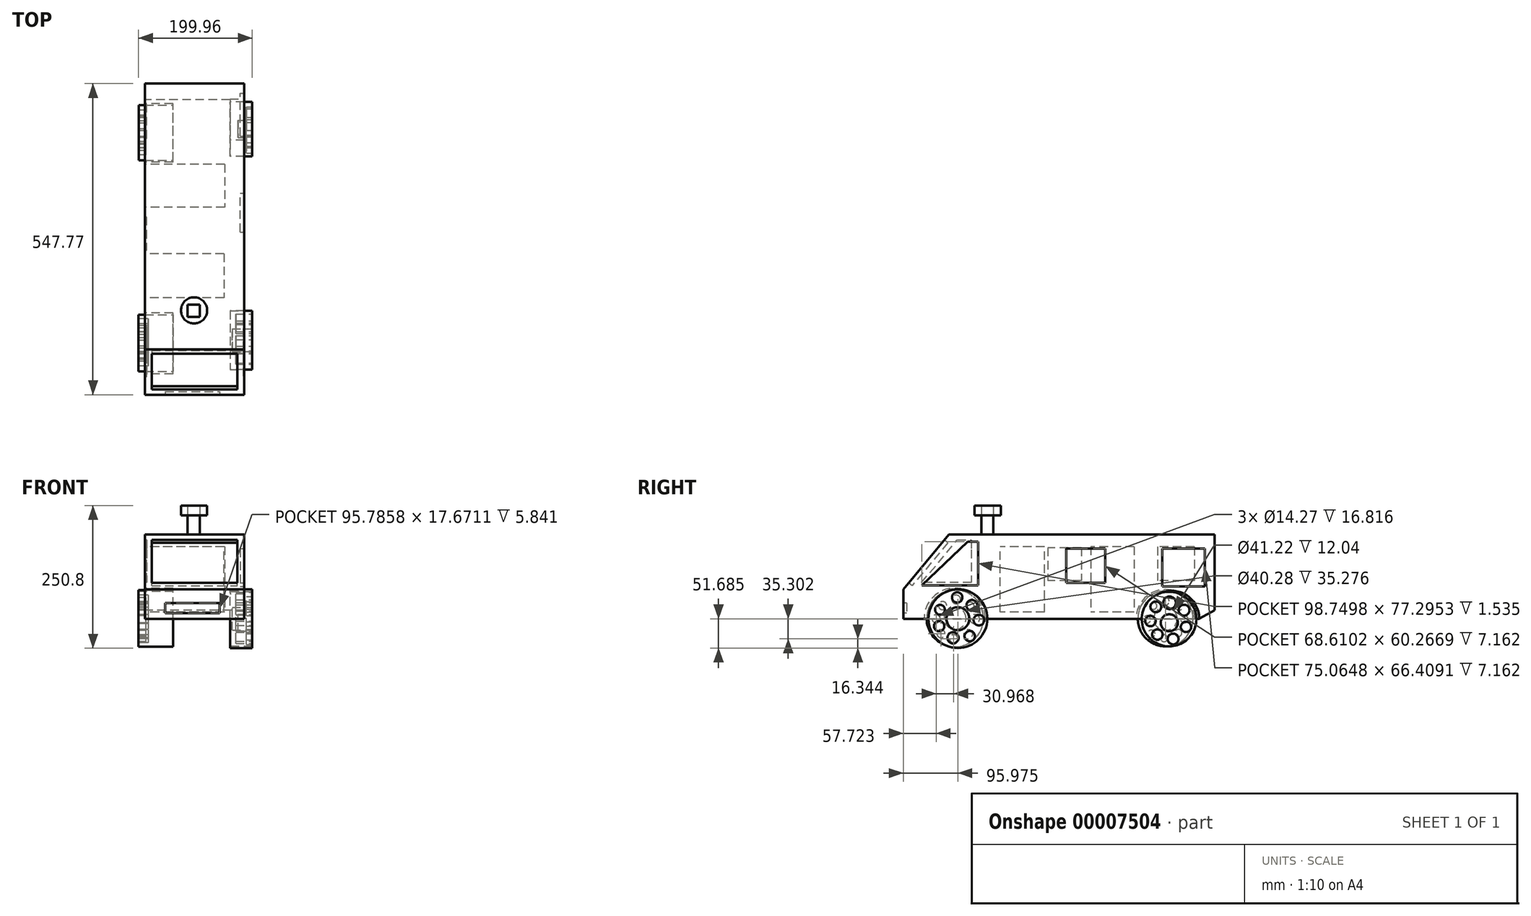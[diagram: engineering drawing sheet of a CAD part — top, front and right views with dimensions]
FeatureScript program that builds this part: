
annotation { "Feature Type Name" : "Feature", "Feature Type Description" : "" }
export const myFeature = defineFeature(function(context is Context, id is Id, definition is map)
    precondition{}
    {
        {
            var Q0;
            Q0=qCreatedBy(makeId("Front.planeOp"),FACE);
            var sketch = newSketch(context, id + "F0", { "sketchPlane" : qUnion([Q0])});
            skLineSegment(sketch, "E0.bottom", {"start": v(74.37, 73.44) * mm, "end": v(-75.3, 73.44) * mm});
            skLineSegment(sketch, "E0.top", {"start": v(74.37, -74.82) * mm, "end": v(-75.3, -74.82) * mm});
            skLineSegment(sketch, "E0.left", {"start": v(74.37, 73.44) * mm, "end": v(74.37, -74.82) * mm});
            skLineSegment(sketch, "E0.right", {"start": v(-75.3, 73.44) * mm, "end": v(-75.3, -74.82) * mm});
            skSolve(sketch);
        }
        {
            var Q0;
            Q0=makeQuery(id+"F0.imprint","IMPRINT",FACE,{"disambiguationData":[TD([[makeQuery(id+"F0.imprint","IMPRINT",EDGE,{"derivedFrom":sQuery(id+"F0.wireOp",EDGE,"E0.bottom")}),1.0]])]});
            extrude(context, id + "F1", {"entities" : qUnion([Q0]), "depth" : 547.77 * mm});
        }
        {
            var Q0;
            Q0=makeQuery(id+"F1.opExtrude","SWEPT_FACE",FACE,{"disambiguationData":[OSD([sQuery(id+"F0.wireOp",EDGE,"E0.right")])]});
            var sketch = newSketch(context, id + "F2", { "sketchPlane" : qUnion([Q0])});
            skCircle(sketch, "E1", {"center": v(86.72, -74.82) * mm, "radius": 51.51 * mm});
            skCircle(sketch, "E2", {"center": v(457.4, -74.82) * mm, "radius": 53.88 * mm});
            skSolve(sketch);
        }
        {
            var Q0;
            {var subQ0=makeQuery(id+"F1.opExtrude","SWEPT_EDGE",EDGE,{"disambiguationData":[OSD([sQuery(id+"F0.wireOp",EDGE,"E0.top"),sQuery(id+"F0.wireOp",EDGE,"E0.right")])]});var subQ1=sQuery(id+"F2.wireOp",EDGE,"E1");var subQ3=makeQuery(id+"F2.imprint","INTERSECT",VERTEX,{"disambiguationData":[OD(0.0)],"derivedFrom":[subQ0,subQ1]});Q0=makeQuery(id+"F2.imprint","IMPRINT",FACE,{"disambiguationData":[TD([[makeQuery(id+"F2.imprint","IMPRINT",EDGE,{"disambiguationData":[TD([[subQ3,-1.0]])],"derivedFrom":subQ1}),1.0]])]});}
            var Q1;
            {var subQ0=makeQuery(id+"F1.opExtrude","SWEPT_EDGE",EDGE,{"disambiguationData":[OSD([sQuery(id+"F0.wireOp",EDGE,"E0.top"),sQuery(id+"F0.wireOp",EDGE,"E0.right")])]});var subQ1=sQuery(id+"F2.wireOp",EDGE,"E1");var subQ3=makeQuery(id+"F2.imprint","INTERSECT",VERTEX,{"disambiguationData":[OD(0.0)],"derivedFrom":[subQ0,subQ1]});Q1=makeQuery(id+"F2.imprint","IMPRINT",FACE,{"disambiguationData":[TD([[makeQuery(id+"F2.imprint","IMPRINT",EDGE,{"disambiguationData":[TD([[subQ3,1.0]])],"derivedFrom":subQ1}),1.0]])]});}
            var Q2;
            {var subQ0=makeQuery(id+"F1.opExtrude","SWEPT_EDGE",EDGE,{"disambiguationData":[OSD([sQuery(id+"F0.wireOp",EDGE,"E0.top"),sQuery(id+"F0.wireOp",EDGE,"E0.right")])]});var subQ1=sQuery(id+"F2.wireOp",EDGE,"E2");var subQ3=makeQuery(id+"F2.imprint","INTERSECT",VERTEX,{"disambiguationData":[OD(0.0)],"derivedFrom":[subQ0,subQ1]});Q2=makeQuery(id+"F2.imprint","IMPRINT",FACE,{"disambiguationData":[TD([[makeQuery(id+"F2.imprint","IMPRINT",EDGE,{"disambiguationData":[TD([[subQ3,1.0]])],"derivedFrom":subQ1}),1.0]])]});}
            var Q3;
            {var subQ0=makeQuery(id+"F1.opExtrude","SWEPT_EDGE",EDGE,{"disambiguationData":[OSD([sQuery(id+"F0.wireOp",EDGE,"E0.top"),sQuery(id+"F0.wireOp",EDGE,"E0.right")])]});var subQ1=sQuery(id+"F2.wireOp",EDGE,"E2");var subQ3=makeQuery(id+"F2.imprint","INTERSECT",VERTEX,{"disambiguationData":[OD(0.0)],"derivedFrom":[subQ0,subQ1]});Q3=makeQuery(id+"F2.imprint","IMPRINT",FACE,{"disambiguationData":[TD([[makeQuery(id+"F2.imprint","IMPRINT",EDGE,{"disambiguationData":[TD([[subQ3,-1.0]])],"derivedFrom":subQ1}),1.0]])]});}
            extrude(context, id + "F3", {"entities" : qUnion([Q0, Q1, Q2, Q3]), "operationType" : NewBodyOperationType.REMOVE, "oppositeDirection" : true, "depth" : 24.2 * mm});
        }
        {
            var Q0;
            Q0=makeQuery(id+"F3.boolean.opBoolean","COPY",FACE,{"derivedFrom":makeQuery(id+"F3.opExtrude","CAP_FACE",FACE,{"disambiguationData":[OSD([sQuery(id+"F2.wireOp",EDGE,"E1")])],"isStart":false})});
            var sketch = newSketch(context, id + "F4", { "sketchPlane" : qUnion([Q0])});
            skCircle(sketch, "E3", {"center": v(86.72, -74.82) * mm, "radius": 48.61 * mm});
            skCircle(sketch, "E4", {"center": v(456.68, -74.24) * mm, "radius": 49.9 * mm});
            skSolve(sketch);
        }
        {
            var Q0;
            {var subQ0=makeQuery(id+"F3.boolean.opBoolean","INTERSECT",EDGE,{"derivedFrom":[makeQuery(id+"F1.opExtrude","SWEPT_FACE",FACE,{"disambiguationData":[OSD([sQuery(id+"F0.wireOp",EDGE,"E0.top")])]}),makeQuery(id+"F3.opExtrude","CAP_FACE",FACE,{"disambiguationData":[OSD([sQuery(id+"F2.wireOp",EDGE,"E1")])],"isStart":false})]});var subQ1=sQuery(id+"F4.wireOp",EDGE,"E3");var subQ3=makeQuery(id+"F4.imprint","INTERSECT",VERTEX,{"disambiguationData":[OD(0.0)],"derivedFrom":[subQ0,subQ1]});Q0=makeQuery(id+"F4.imprint","IMPRINT",FACE,{"disambiguationData":[TD([[makeQuery(id+"F4.imprint","IMPRINT",EDGE,{"disambiguationData":[TD([[subQ3,1.0]])],"derivedFrom":subQ1}),1.0]])]});}
            var Q1;
            {var subQ0=makeQuery(id+"F3.boolean.opBoolean","INTERSECT",EDGE,{"derivedFrom":[makeQuery(id+"F1.opExtrude","SWEPT_FACE",FACE,{"disambiguationData":[OSD([sQuery(id+"F0.wireOp",EDGE,"E0.top")])]}),makeQuery(id+"F3.opExtrude","CAP_FACE",FACE,{"disambiguationData":[OSD([sQuery(id+"F2.wireOp",EDGE,"E1")])],"isStart":false})]});var subQ1=sQuery(id+"F4.wireOp",EDGE,"E3");var subQ3=makeQuery(id+"F4.imprint","INTERSECT",VERTEX,{"disambiguationData":[OD(0.0)],"derivedFrom":[subQ0,subQ1]});Q1=makeQuery(id+"F4.imprint","IMPRINT",FACE,{"disambiguationData":[TD([[makeQuery(id+"F4.imprint","IMPRINT",EDGE,{"disambiguationData":[TD([[subQ3,-1.0]])],"derivedFrom":subQ1}),1.0]])]});}
            var Q2;
            Q2=makeQuery(id+"F4.imprint","IMPRINT",FACE,{"disambiguationData":[TD([[makeQuery(id+"F4.imprint","IMPRINT",EDGE,{"derivedFrom":sQuery(id+"F4.wireOp",EDGE,"E4")}),1.0]])]});
            extrude(context, id + "F5", {"entities" : qUnion([Q0, Q1, Q2]), "operationType" : NewBodyOperationType.ADD, "depth" : 40.9 * mm});
        }
        {
            var Q0;
            Q0=makeQuery(id+"F1.opExtrude","SWEPT_FACE",FACE,{"disambiguationData":[OSD([sQuery(id+"F0.wireOp",EDGE,"E0.left")])]});
            var sketch = newSketch(context, id + "F6", { "sketchPlane" : qUnion([Q0])});
            skCircle(sketch, "E5", {"center": v(-451.8, -74.82) * mm, "radius": 51.88 * mm});
            skCircle(sketch, "E6", {"center": v(-76.52, -74.82) * mm, "radius": 49.33 * mm});
            skSolve(sketch);
        }
        {
            var Q0;
            {var subQ0=makeQuery(id+"F1.opExtrude","SWEPT_EDGE",EDGE,{"disambiguationData":[OSD([sQuery(id+"F0.wireOp",EDGE,"E0.top"),sQuery(id+"F0.wireOp",EDGE,"E0.left")])]});var subQ1=sQuery(id+"F6.wireOp",EDGE,"E5");var subQ3=makeQuery(id+"F6.imprint","INTERSECT",VERTEX,{"disambiguationData":[OD(0.0)],"derivedFrom":[subQ0,subQ1]});Q0=makeQuery(id+"F6.imprint","IMPRINT",FACE,{"disambiguationData":[TD([[makeQuery(id+"F6.imprint","IMPRINT",EDGE,{"disambiguationData":[TD([[subQ3,1.0]])],"derivedFrom":subQ1}),1.0]])]});}
            var Q1;
            {var subQ0=makeQuery(id+"F1.opExtrude","SWEPT_EDGE",EDGE,{"disambiguationData":[OSD([sQuery(id+"F0.wireOp",EDGE,"E0.top"),sQuery(id+"F0.wireOp",EDGE,"E0.left")])]});var subQ1=sQuery(id+"F6.wireOp",EDGE,"E6");var subQ3=makeQuery(id+"F6.imprint","INTERSECT",VERTEX,{"disambiguationData":[OD(0.0)],"derivedFrom":[subQ0,subQ1]});Q1=makeQuery(id+"F6.imprint","IMPRINT",FACE,{"disambiguationData":[TD([[makeQuery(id+"F6.imprint","IMPRINT",EDGE,{"disambiguationData":[TD([[subQ3,-1.0]])],"derivedFrom":subQ1}),1.0]])]});}
            var Q2;
            {var subQ0=makeQuery(id+"F1.opExtrude","SWEPT_EDGE",EDGE,{"disambiguationData":[OSD([sQuery(id+"F0.wireOp",EDGE,"E0.top"),sQuery(id+"F0.wireOp",EDGE,"E0.left")])]});var subQ1=sQuery(id+"F6.wireOp",EDGE,"E6");var subQ3=makeQuery(id+"F6.imprint","INTERSECT",VERTEX,{"disambiguationData":[OD(0.0)],"derivedFrom":[subQ0,subQ1]});Q2=makeQuery(id+"F6.imprint","IMPRINT",FACE,{"disambiguationData":[TD([[makeQuery(id+"F6.imprint","IMPRINT",EDGE,{"disambiguationData":[TD([[subQ3,1.0]])],"derivedFrom":subQ1}),1.0]])]});}
            var Q3;
            {var subQ0=makeQuery(id+"F1.opExtrude","SWEPT_EDGE",EDGE,{"disambiguationData":[OSD([sQuery(id+"F0.wireOp",EDGE,"E0.top"),sQuery(id+"F0.wireOp",EDGE,"E0.left")])]});var subQ1=sQuery(id+"F6.wireOp",EDGE,"E5");var subQ3=makeQuery(id+"F6.imprint","INTERSECT",VERTEX,{"disambiguationData":[OD(0.0)],"derivedFrom":[subQ0,subQ1]});Q3=makeQuery(id+"F6.imprint","IMPRINT",FACE,{"disambiguationData":[TD([[makeQuery(id+"F6.imprint","IMPRINT",EDGE,{"disambiguationData":[TD([[subQ3,-1.0]])],"derivedFrom":subQ1}),1.0]])]});}
            extrude(context, id + "F7", {"entities" : qUnion([Q0, Q1, Q2, Q3]), "operationType" : NewBodyOperationType.REMOVE, "oppositeDirection" : true, "depth" : 25 * mm});
        }
        {
            var Q0;
            Q0=makeQuery(id+"F7.boolean.opBoolean","COPY",FACE,{"derivedFrom":makeQuery(id+"F7.opExtrude","CAP_FACE",FACE,{"disambiguationData":[OSD([sQuery(id+"F6.wireOp",EDGE,"E5")])],"isStart":false})});
            var sketch = newSketch(context, id + "F8", { "sketchPlane" : qUnion([Q0])});
            skCircle(sketch, "E7", {"center": v(-451.8, -74.82) * mm, "radius": 51.69 * mm});
            skCircle(sketch, "E8", {"center": v(-80.35, -75.29) * mm, "radius": 48.09 * mm});
            skSolve(sketch);
        }
        {
            var Q0;
            {var subQ0=makeQuery(id+"F7.boolean.opBoolean","INTERSECT",EDGE,{"derivedFrom":[makeQuery(id+"F1.opExtrude","SWEPT_FACE",FACE,{"disambiguationData":[OSD([sQuery(id+"F0.wireOp",EDGE,"E0.top")])]}),makeQuery(id+"F7.opExtrude","CAP_FACE",FACE,{"disambiguationData":[OSD([sQuery(id+"F6.wireOp",EDGE,"E5")])],"isStart":false})]});var subQ1=sQuery(id+"F8.wireOp",EDGE,"E7");var subQ3=makeQuery(id+"F8.imprint","INTERSECT",VERTEX,{"disambiguationData":[OD(0.0)],"derivedFrom":[subQ0,subQ1]});Q0=makeQuery(id+"F8.imprint","IMPRINT",FACE,{"disambiguationData":[TD([[makeQuery(id+"F8.imprint","IMPRINT",EDGE,{"disambiguationData":[TD([[subQ3,-1.0]])],"derivedFrom":subQ1}),1.0]])]});}
            var Q1;
            {var subQ0=makeQuery(id+"F7.boolean.opBoolean","INTERSECT",EDGE,{"derivedFrom":[makeQuery(id+"F1.opExtrude","SWEPT_FACE",FACE,{"disambiguationData":[OSD([sQuery(id+"F0.wireOp",EDGE,"E0.top")])]}),makeQuery(id+"F7.opExtrude","CAP_FACE",FACE,{"disambiguationData":[OSD([sQuery(id+"F6.wireOp",EDGE,"E5")])],"isStart":false})]});var subQ1=sQuery(id+"F8.wireOp",EDGE,"E7");var subQ3=makeQuery(id+"F8.imprint","INTERSECT",VERTEX,{"disambiguationData":[OD(0.0)],"derivedFrom":[subQ0,subQ1]});Q1=makeQuery(id+"F8.imprint","IMPRINT",FACE,{"disambiguationData":[TD([[makeQuery(id+"F8.imprint","IMPRINT",EDGE,{"disambiguationData":[TD([[subQ3,1.0]])],"derivedFrom":subQ1}),1.0]])]});}
            var Q2;
            Q2=makeQuery(id+"F8.imprint","IMPRINT",FACE,{"disambiguationData":[TD([[makeQuery(id+"F8.imprint","IMPRINT",EDGE,{"derivedFrom":sQuery(id+"F8.wireOp",EDGE,"E8")}),1.0]])]});
            extrude(context, id + "F9", {"entities" : qUnion([Q0, Q1, Q2]), "operationType" : NewBodyOperationType.ADD, "depth" : 39 * mm});
        }
        {
            var Q0;
            Q0=makeQuery(id+"F1.opExtrude","SWEPT_FACE",FACE,{"disambiguationData":[OSD([sQuery(id+"F0.wireOp",EDGE,"E0.right")])]});
            var sketch = newSketch(context, id + "F10", { "sketchPlane" : qUnion([Q0])});
            skLineSegment(sketch, "E9", {"start": v(467.77, 73.44) * mm, "end": v(547.77, -22.84) * mm});
            skLineSegment(sketch, "E10", {"start": v(547.77, -22.84) * mm, "end": v(547.77, 73.44) * mm});
            skLineSegment(sketch, "E11", {"start": v(547.77, 73.44) * mm, "end": v(467.77, 73.44) * mm});
            skSolve(sketch);
        }
        {
            var Q0;
            Q0=makeQuery(id+"F10.imprint","IMPRINT",FACE,{"disambiguationData":[TD([[makeQuery(id+"F10.imprint","IMPRINT",EDGE,{"derivedFrom":sQuery(id+"F10.wireOp",EDGE,"E9")}),1.0]])]});
            extrude(context, id + "F11", {"entities" : qUnion([Q0]), "operationType" : NewBodyOperationType.REMOVE, "oppositeDirection" : true, "depth" : 194.14 * mm});
        }
        {
            var Q0;
            Q0=makeQuery(id+"F1.opExtrude","SWEPT_FACE",FACE,{"disambiguationData":[OSD([sQuery(id+"F0.wireOp",EDGE,"E0.right")])]});
            var sketch = newSketch(context, id + "F12", { "sketchPlane" : qUnion([Q0])});
            skSolve(sketch);
        }
        {
            var Q0;
            {var subQ0=sQuery(id+"F0.wireOp",EDGE,"E0.right");Q0=makeQuery(id+"F12.imprint","IMPRINT",FACE,{"disambiguationData":[TD([[makeQuery(id+"F12.imprint","IMPRINT",EDGE,{"derivedFrom":makeQuery(id+"F1.opExtrude","CAP_EDGE",EDGE,{"disambiguationData":[OSD([subQ0])],"isStart":true})}),1.0]])]});}
            var sketch = newSketch(context, id + "F13", { "sketchPlane" : qUnion([Q0])});
            skLineSegment(sketch, "E12.bottom", {"start": v(299.28, -63.26) * mm, "end": v(377.16, -63.26) * mm});
            skLineSegment(sketch, "E12.top", {"start": v(299.28, 51.97) * mm, "end": v(377.16, 51.97) * mm});
            skLineSegment(sketch, "E12.left", {"start": v(299.28, -63.26) * mm, "end": v(299.28, 51.97) * mm});
            skLineSegment(sketch, "E12.right", {"start": v(377.16, -63.26) * mm, "end": v(377.16, 51.97) * mm});
            skSolve(sketch);
        }
        {
            var Q0;
            Q0=makeQuery(id+"F13.imprint","IMPRINT",FACE,{"disambiguationData":[TD([[makeQuery(id+"F13.imprint","IMPRINT",EDGE,{"derivedFrom":sQuery(id+"F13.wireOp",EDGE,"E12.bottom")}),1.0]])]});
            extrude(context, id + "F14", {"entities" : qUnion([Q0]), "operationType" : NewBodyOperationType.REMOVE, "oppositeDirection" : true, "depth" : 147.5 * mm});
        }
        {
            var Q0;
            Q0=makeQuery(id+"F1.opExtrude","SWEPT_FACE",FACE,{"disambiguationData":[OSD([sQuery(id+"F0.wireOp",EDGE,"E0.right")])]});
            extrude(context, id + "F15", {"entities" : qUnion([Q0]), "operationType" : NewBodyOperationType.ADD, "depth" : 25 * mm});
        }
        {
            var Q0;
            Q0=makeQuery(id+"F15.opExtrude","CAP_FACE",FACE,{"disambiguationData":[OSD([sQuery(id+"F0.wireOp",EDGE,"E0.right")])],"isStart":false});
            var sketch = newSketch(context, id + "F16", { "sketchPlane" : qUnion([Q0])});
            skLineSegment(sketch, "E13.bottom", {"start": v(141.83, 51.97) * mm, "end": v(217.84, 51.97) * mm});
            skLineSegment(sketch, "E13.top", {"start": v(141.83, -63.26) * mm, "end": v(217.84, -63.26) * mm});
            skLineSegment(sketch, "E13.left", {"start": v(141.83, 51.97) * mm, "end": v(141.83, -63.26) * mm});
            skLineSegment(sketch, "E13.right", {"start": v(217.84, 51.97) * mm, "end": v(217.84, -63.26) * mm});
            skSolve(sketch);
        }
        {
            var Q0;
            Q0=makeQuery(id+"F16.imprint","IMPRINT",FACE,{"disambiguationData":[TD([[makeQuery(id+"F16.imprint","IMPRINT",EDGE,{"derivedFrom":sQuery(id+"F16.wireOp",EDGE,"E13.bottom")}),-1.0]])]});
            extrude(context, id + "F17", {"entities" : qUnion([Q0]), "operationType" : NewBodyOperationType.REMOVE, "oppositeDirection" : true, "depth" : 173.86 * mm});
        }
        {
            var Q0;
            Q0=makeQuery(id+"F5.opExtrude","CAP_FACE",FACE,{"disambiguationData":[OSD([sQuery(id+"F4.wireOp",EDGE,"E3")])],"isStart":false});
            extrude(context, id + "F18", {"entities" : qUnion([Q0]), "operationType" : NewBodyOperationType.ADD, "depth" : 19.4 * mm});
        }
        {
            var Q0;
            Q0=makeQuery(id+"F5.opExtrude","CAP_FACE",FACE,{"disambiguationData":[OSD([sQuery(id+"F4.wireOp",EDGE,"E4")])],"isStart":false});
            extrude(context, id + "F19", {"entities" : qUnion([Q0]), "operationType" : NewBodyOperationType.ADD, "depth" : 19.6 * mm});
        }
        {
            var Q0;
            {var subQ0=sQuery(id+"F10.wireOp",EDGE,"E9");Q0=makeQuery(id+"F15.boolean.opBoolean","MERGE",FACE,{"derivedFrom":[makeQuery(id+"F11.boolean.opBoolean","COPY",FACE,{"derivedFrom":makeQuery(id+"F11.opExtrude","SWEPT_FACE",FACE,{"disambiguationData":[OSD([subQ0])]})}),makeQuery(id+"F15.opExtrude","SWEPT_FACE",FACE,{"disambiguationData":[OSD([subQ0])]})]});}
            var sketch = newSketch(context, id + "F20", { "sketchPlane" : qUnion([Q0])});
            skLineSegment(sketch, "E14.bottom", {"start": v(-88.12, -254.66) * mm, "end": v(62.1, -254.66) * mm});
            skLineSegment(sketch, "E14.top", {"start": v(-88.12, -353.33) * mm, "end": v(62.1, -353.33) * mm});
            skLineSegment(sketch, "E14.left", {"start": v(-88.12, -254.66) * mm, "end": v(-88.12, -353.33) * mm});
            skLineSegment(sketch, "E14.right", {"start": v(62.1, -254.66) * mm, "end": v(62.1, -353.33) * mm});
            skSolve(sketch);
        }
        {
            var Q0;
            Q0=makeQuery(id+"F20.imprint","IMPRINT",FACE,{"disambiguationData":[TD([[makeQuery(id+"F20.imprint","IMPRINT",EDGE,{"derivedFrom":sQuery(id+"F20.wireOp",EDGE,"E14.bottom")}),-1.0]])]});
            extrude(context, id + "F21", {"entities" : qUnion([Q0]), "operationType" : NewBodyOperationType.REMOVE, "oppositeDirection" : true, "depth" : 7.95 * mm});
        }
        {
            var Q0;
            Q0=makeQuery(id+"F17.boolean.opBoolean","COPY",FACE,{"derivedFrom":makeQuery(id+"F17.opExtrude","CAP_FACE",FACE,{"disambiguationData":[OSD([sQuery(id+"F16.wireOp",EDGE,"E13.bottom"),sQuery(id+"F16.wireOp",EDGE,"E13.top"),sQuery(id+"F16.wireOp",EDGE,"E13.left"),sQuery(id+"F16.wireOp",EDGE,"E13.right")])],"isStart":false})});
            var sketch = newSketch(context, id + "F22", { "sketchPlane" : qUnion([Q0])});
            skLineSegment(sketch, "E15.bottom", {"start": v(217.84, 51.97) * mm, "end": v(141.83, 51.97) * mm});
            skLineSegment(sketch, "E15.top", {"start": v(217.84, -63.26) * mm, "end": v(141.83, -63.26) * mm});
            skLineSegment(sketch, "E15.left", {"start": v(217.84, 51.97) * mm, "end": v(217.84, -63.26) * mm});
            skLineSegment(sketch, "E15.right", {"start": v(141.83, 51.97) * mm, "end": v(141.83, -63.26) * mm});
            skSolve(sketch);
        }
        {
            var Q0;
            Q0=makeQuery(id+"F14.boolean.opBoolean","COPY",FACE,{"derivedFrom":makeQuery(id+"F14.opExtrude","CAP_FACE",FACE,{"disambiguationData":[OSD([sQuery(id+"F13.wireOp",EDGE,"E12.bottom"),sQuery(id+"F13.wireOp",EDGE,"E12.top"),sQuery(id+"F13.wireOp",EDGE,"E12.left"),sQuery(id+"F13.wireOp",EDGE,"E12.right")])],"isStart":false})});
            var sketch = newSketch(context, id + "F23", { "sketchPlane" : qUnion([Q0])});
            skLineSegment(sketch, "E16.bottom", {"start": v(377.16, 51.97) * mm, "end": v(299.28, 51.97) * mm});
            skLineSegment(sketch, "E16.top", {"start": v(377.16, -63.26) * mm, "end": v(299.28, -63.26) * mm});
            skLineSegment(sketch, "E16.left", {"start": v(377.16, 51.97) * mm, "end": v(377.16, -63.26) * mm});
            skLineSegment(sketch, "E16.right", {"start": v(299.28, 51.97) * mm, "end": v(299.28, -63.26) * mm});
            skSolve(sketch);
        }
        {
            var Q0;
            Q0=makeQuery(id+"F23.imprint","IMPRINT",FACE,{"disambiguationData":[TD([[makeQuery(id+"F23.imprint","IMPRINT",EDGE,{"derivedFrom":sQuery(id+"F23.wireOp",EDGE,"E16.bottom")}),-1.0]])]});
            var Q1;
            Q1=makeQuery(id+"F22.imprint","IMPRINT",FACE,{"disambiguationData":[TD([[makeQuery(id+"F22.imprint","IMPRINT",EDGE,{"derivedFrom":sQuery(id+"F22.wireOp",EDGE,"E15.bottom")}),-1.0]])]});
            extrude(context, id + "F24", {"entities" : qUnion([Q0, Q1]), "operationType" : NewBodyOperationType.ADD, "depth" : 33.55 * mm});
        }
        {
            var Q0;
            {var subQ0=sQuery(id+"F0.wireOp",EDGE,"E0.bottom");Q0=makeQuery(id+"F15.boolean.opBoolean","MERGE",FACE,{"derivedFrom":[makeQuery(id+"F1.opExtrude","SWEPT_FACE",FACE,{"disambiguationData":[OSD([subQ0])]}),makeQuery(id+"F15.opExtrude","SWEPT_FACE",FACE,{"disambiguationData":[OSD([subQ0,sQuery(id+"F0.wireOp",EDGE,"E0.right")])]})]});}
            var sketch = newSketch(context, id + "F25", { "sketchPlane" : qUnion([Q0])});
            skLineSegment(sketch, "E17.bottom", {"start": v(-4.06, -389.3) * mm, "end": v(-25.31, -389.3) * mm});
            skLineSegment(sketch, "E17.top", {"start": v(-4.06, -410.41) * mm, "end": v(-25.31, -410.41) * mm});
            skLineSegment(sketch, "E17.left", {"start": v(-4.06, -389.3) * mm, "end": v(-4.06, -410.41) * mm});
            skLineSegment(sketch, "E17.right", {"start": v(-25.31, -389.3) * mm, "end": v(-25.31, -410.41) * mm});
            skSolve(sketch);
        }
        {
            var Q0;
            Q0=makeQuery(id+"F25.imprint","IMPRINT",FACE,{"disambiguationData":[TD([[makeQuery(id+"F25.imprint","IMPRINT",EDGE,{"derivedFrom":sQuery(id+"F25.wireOp",EDGE,"E17.bottom")}),1.0]])]});
            extrude(context, id + "F26", {"entities" : qUnion([Q0]), "operationType" : NewBodyOperationType.ADD, "depth" : 33.85 * mm});
        }
        {
            var Q0;
            Q0=makeQuery(id+"F26.opExtrude","CAP_FACE",FACE,{"disambiguationData":[OSD([sQuery(id+"F25.wireOp",EDGE,"E17.bottom"),sQuery(id+"F25.wireOp",EDGE,"E17.top"),sQuery(id+"F25.wireOp",EDGE,"E17.left"),sQuery(id+"F25.wireOp",EDGE,"E17.right")])],"isStart":false});
            var sketch = newSketch(context, id + "F27", { "sketchPlane" : qUnion([Q0])});
            skCircle(sketch, "E18", {"center": v(-13.96, -399.18) * mm, "radius": 23.07 * mm});
            skSolve(sketch);
        }
        {
            var Q0;
            Q0=makeQuery(id+"F27.imprint","IMPRINT",FACE,{"disambiguationData":[TD([[makeQuery(id+"F27.imprint","IMPRINT",EDGE,{"derivedFrom":sQuery(id+"F27.wireOp",EDGE,"E18")}),1.0]])]});
            extrude(context, id + "F28", {"entities" : qUnion([Q0]), "depth" : 17 * mm});
        }
        {
            var Q0;
            {var subQ0=sQuery(id+"F0.wireOp",EDGE,"E0.right");Q0=makeQuery(id+"F15.boolean.opBoolean","MERGE",FACE,{"derivedFrom":[makeQuery(id+"F1.opExtrude","CAP_FACE",FACE,{"disambiguationData":[OSD([sQuery(id+"F0.wireOp",EDGE,"E0.bottom"),sQuery(id+"F0.wireOp",EDGE,"E0.top"),sQuery(id+"F0.wireOp",EDGE,"E0.left"),subQ0])],"isStart":false}),makeQuery(id+"F15.opExtrude","SWEPT_FACE",FACE,{"disambiguationData":[OSD([subQ0]),TDD([makeQuery(id+"F1.opExtrude","CAP_EDGE",EDGE,{"disambiguationData":[OSD([subQ0])],"isStart":false})])]})]});}
            var sketch = newSketch(context, id + "F29", { "sketchPlane" : qUnion([Q0])});
            skLineSegment(sketch, "E19.bottom", {"start": v(-64.55, -47) * mm, "end": v(31.24, -47) * mm});
            skLineSegment(sketch, "E19.top", {"start": v(-64.55, -64.68) * mm, "end": v(31.24, -64.68) * mm});
            skLineSegment(sketch, "E19.left", {"start": v(-64.55, -47) * mm, "end": v(-64.55, -64.68) * mm});
            skLineSegment(sketch, "E19.right", {"start": v(31.24, -47) * mm, "end": v(31.24, -64.68) * mm});
            skSolve(sketch);
        }
        {
            var Q0;
            Q0=makeQuery(id+"F29.imprint","IMPRINT",FACE,{"disambiguationData":[TD([[makeQuery(id+"F29.imprint","IMPRINT",EDGE,{"derivedFrom":sQuery(id+"F29.wireOp",EDGE,"E19.bottom")}),-1.0]])]});
            extrude(context, id + "F30", {"entities" : qUnion([Q0]), "operationType" : NewBodyOperationType.REMOVE, "oppositeDirection" : true, "depth" : 5.84 * mm});
        }
        {
            var Q0;
            Q0=makeQuery(id+"F26.opExtrude","CAP_FACE",FACE,{"disambiguationData":[OSD([sQuery(id+"F25.wireOp",EDGE,"E17.bottom"),sQuery(id+"F25.wireOp",EDGE,"E17.top"),sQuery(id+"F25.wireOp",EDGE,"E17.left"),sQuery(id+"F25.wireOp",EDGE,"E17.right")])],"isStart":false});
            var sketch = newSketch(context, id + "F31", { "sketchPlane" : qUnion([Q0])});
            skLineSegment(sketch, "E20.bottom", {"start": v(-4.06, -389.3) * mm, "end": v(-25.31, -389.3) * mm});
            skLineSegment(sketch, "E20.top", {"start": v(-4.06, -410.41) * mm, "end": v(-25.31, -410.41) * mm});
            skLineSegment(sketch, "E20.left", {"start": v(-4.06, -389.3) * mm, "end": v(-4.06, -410.41) * mm});
            skLineSegment(sketch, "E20.right", {"start": v(-25.31, -389.3) * mm, "end": v(-25.31, -410.41) * mm});
            skSolve(sketch);
        }
        {
            var Q0;
            Q0=makeQuery(id+"F31.imprint","IMPRINT",FACE,{"disambiguationData":[TD([[makeQuery(id+"F31.imprint","IMPRINT",EDGE,{"derivedFrom":sQuery(id+"F31.wireOp",EDGE,"E20.bottom")}),1.0]])]});
            extrude(context, id + "F32", {"entities" : qUnion([Q0]), "depth" : 15.6 * mm});
        }
        {
            var Q0;
            Q0=makeQuery(id+"F18.opExtrude","CAP_FACE",FACE,{"disambiguationData":[OSD([sQuery(id+"F4.wireOp",EDGE,"E3")])],"isStart":false});
            var sketch = newSketch(context, id + "F33", { "sketchPlane" : qUnion([Q0])});
            skCircle(sketch, "E21", {"center": v(86.72, -74.82) * mm, "radius": 20.6 * mm});
            skCircle(sketch, "E22", {"center": v(86.72, -44.17) * mm, "radius": 6.58 * mm});
            skCircle(sketch, "E23", {"center": v(107.76, -52.27) * mm, "radius": 5.93 * mm});
            skCircle(sketch, "E24", {"center": v(119.16, -76.12) * mm, "radius": 6.52 * mm});
            skCircle(sketch, "E25", {"center": v(111.65, -101.35) * mm, "radius": 6.5 * mm});
            skCircle(sketch, "E26", {"center": v(89.08, -109.16) * mm, "radius": 6.09 * mm});
            skCircle(sketch, "E27", {"center": v(63.84, -99.8) * mm, "radius": 6.09 * mm});
            skCircle(sketch, "E28", {"center": v(53.63, -75.4) * mm, "radius": 6.52 * mm});
            skCircle(sketch, "E29", {"center": v(62.87, -52.55) * mm, "radius": 7.1 * mm});
            skSolve(sketch);
        }
        {
            var Q0;
            Q0=makeQuery(id+"F33.imprint","IMPRINT",FACE,{"disambiguationData":[TD([[makeQuery(id+"F33.imprint","IMPRINT",EDGE,{"derivedFrom":sQuery(id+"F33.wireOp",EDGE,"E25")}),1.0]])]});
            var Q1;
            Q1=makeQuery(id+"F33.imprint","IMPRINT",FACE,{"disambiguationData":[TD([[makeQuery(id+"F33.imprint","IMPRINT",EDGE,{"derivedFrom":sQuery(id+"F33.wireOp",EDGE,"E28")}),1.0]])]});
            var Q2;
            Q2=makeQuery(id+"F33.imprint","IMPRINT",FACE,{"disambiguationData":[TD([[makeQuery(id+"F33.imprint","IMPRINT",EDGE,{"derivedFrom":sQuery(id+"F33.wireOp",EDGE,"E21")}),1.0]])]});
            var Q3;
            Q3=makeQuery(id+"F33.imprint","IMPRINT",FACE,{"disambiguationData":[TD([[makeQuery(id+"F33.imprint","IMPRINT",EDGE,{"derivedFrom":sQuery(id+"F33.wireOp",EDGE,"E23")}),1.0]])]});
            var Q4;
            Q4=makeQuery(id+"F33.imprint","IMPRINT",FACE,{"disambiguationData":[TD([[makeQuery(id+"F33.imprint","IMPRINT",EDGE,{"derivedFrom":sQuery(id+"F33.wireOp",EDGE,"E26")}),1.0]])]});
            var Q5;
            Q5=makeQuery(id+"F33.imprint","IMPRINT",FACE,{"disambiguationData":[TD([[makeQuery(id+"F33.imprint","IMPRINT",EDGE,{"derivedFrom":sQuery(id+"F33.wireOp",EDGE,"E22")}),1.0]])]});
            var Q6;
            Q6=makeQuery(id+"F33.imprint","IMPRINT",FACE,{"disambiguationData":[TD([[makeQuery(id+"F33.imprint","IMPRINT",EDGE,{"derivedFrom":sQuery(id+"F33.wireOp",EDGE,"E29")}),1.0]])]});
            var Q7;
            Q7=makeQuery(id+"F33.imprint","IMPRINT",FACE,{"disambiguationData":[TD([[makeQuery(id+"F33.imprint","IMPRINT",EDGE,{"derivedFrom":sQuery(id+"F33.wireOp",EDGE,"E27")}),1.0]])]});
            var Q8;
            Q8=makeQuery(id+"F33.imprint","IMPRINT",FACE,{"disambiguationData":[TD([[makeQuery(id+"F33.imprint","IMPRINT",EDGE,{"derivedFrom":sQuery(id+"F33.wireOp",EDGE,"E24")}),1.0]])]});
            extrude(context, id + "F34", {"entities" : qUnion([Q0, Q1, Q2, Q3, Q4, Q5, Q6, Q7, Q8]), "operationType" : NewBodyOperationType.REMOVE, "oppositeDirection" : true, "depth" : 12.04 * mm});
        }
        {
            var Q0;
            Q0=makeQuery(id+"F19.opExtrude","CAP_FACE",FACE,{"disambiguationData":[OSD([sQuery(id+"F4.wireOp",EDGE,"E4")])],"isStart":false});
            var sketch = newSketch(context, id + "F35", { "sketchPlane" : qUnion([Q0])});
            skCircle(sketch, "E30", {"center": v(456.68, -74.24) * mm, "radius": 19.32 * mm});
            skCircle(sketch, "E31", {"center": v(454.82, -40.87) * mm, "radius": 7.6 * mm});
            skCircle(sketch, "E32", {"center": v(478.62, -51.74) * mm, "radius": 7.24 * mm});
            skCircle(sketch, "E33", {"center": v(490.05, -74.86) * mm, "radius": 7.13 * mm});
            skCircle(sketch, "E34", {"center": v(481.58, -101.06) * mm, "radius": 7.13 * mm});
            skCircle(sketch, "E35", {"center": v(459.08, -110.17) * mm, "radius": 7.13 * mm});
            skCircle(sketch, "E36", {"center": v(433.73, -102.1) * mm, "radius": 8.02 * mm});
            skCircle(sketch, "E37", {"center": v(422, -75.44) * mm, "radius": 8.17 * mm});
            skCircle(sketch, "E38", {"center": v(429.88, -52.86) * mm, "radius": 6.97 * mm});
            skSolve(sketch);
        }
        {
            var Q0;
            Q0=makeQuery(id+"F35.imprint","IMPRINT",FACE,{"disambiguationData":[TD([[makeQuery(id+"F35.imprint","IMPRINT",EDGE,{"derivedFrom":sQuery(id+"F35.wireOp",EDGE,"E38")}),1.0]])]});
            var Q1;
            Q1=makeQuery(id+"F35.imprint","IMPRINT",FACE,{"disambiguationData":[TD([[makeQuery(id+"F35.imprint","IMPRINT",EDGE,{"derivedFrom":sQuery(id+"F35.wireOp",EDGE,"E30")}),1.0]])]});
            var Q2;
            Q2=makeQuery(id+"F35.imprint","IMPRINT",FACE,{"disambiguationData":[TD([[makeQuery(id+"F35.imprint","IMPRINT",EDGE,{"derivedFrom":sQuery(id+"F35.wireOp",EDGE,"E33")}),1.0]])]});
            var Q3;
            Q3=makeQuery(id+"F35.imprint","IMPRINT",FACE,{"disambiguationData":[TD([[makeQuery(id+"F35.imprint","IMPRINT",EDGE,{"derivedFrom":sQuery(id+"F35.wireOp",EDGE,"E37")}),1.0]])]});
            var Q4;
            Q4=makeQuery(id+"F35.imprint","IMPRINT",FACE,{"disambiguationData":[TD([[makeQuery(id+"F35.imprint","IMPRINT",EDGE,{"derivedFrom":sQuery(id+"F35.wireOp",EDGE,"E35")}),1.0]])]});
            var Q5;
            Q5=makeQuery(id+"F35.imprint","IMPRINT",FACE,{"disambiguationData":[TD([[makeQuery(id+"F35.imprint","IMPRINT",EDGE,{"derivedFrom":sQuery(id+"F35.wireOp",EDGE,"E32")}),1.0]])]});
            var Q6;
            Q6=makeQuery(id+"F35.imprint","IMPRINT",FACE,{"disambiguationData":[TD([[makeQuery(id+"F35.imprint","IMPRINT",EDGE,{"derivedFrom":sQuery(id+"F35.wireOp",EDGE,"E36")}),1.0]])]});
            var Q7;
            Q7=makeQuery(id+"F35.imprint","IMPRINT",FACE,{"disambiguationData":[TD([[makeQuery(id+"F35.imprint","IMPRINT",EDGE,{"derivedFrom":sQuery(id+"F35.wireOp",EDGE,"E31")}),1.0]])]});
            var Q8;
            Q8=makeQuery(id+"F35.imprint","IMPRINT",FACE,{"disambiguationData":[TD([[makeQuery(id+"F35.imprint","IMPRINT",EDGE,{"derivedFrom":sQuery(id+"F35.wireOp",EDGE,"E34")}),1.0]])]});
            extrude(context, id + "F36", {"entities" : qUnion([Q0, Q1, Q2, Q3, Q4, Q5, Q6, Q7, Q8]), "operationType" : NewBodyOperationType.REMOVE, "oppositeDirection" : true, "depth" : 16.82 * mm});
        }
        {
            var Q0;
            Q0=makeQuery(id+"F15.opExtrude","CAP_FACE",FACE,{"disambiguationData":[OSD([sQuery(id+"F0.wireOp",EDGE,"E0.right")])],"isStart":false});
            var sketch = newSketch(context, id + "F37", { "sketchPlane" : qUnion([Q0])});
            skLineSegment(sketch, "E39", {"start": v(427.93, 46.8) * mm, "end": v(427.93, -11.25) * mm});
            skLineSegment(sketch, "E40", {"start": v(427.93, -11.25) * mm, "end": v(515.8, -11.25) * mm});
            skLineSegment(sketch, "E41", {"start": v(515.8, -11.25) * mm, "end": v(452.8, 63.7) * mm});
            skLineSegment(sketch, "E42", {"start": v(452.8, 63.7) * mm, "end": v(428.08, 63.7) * mm});
            skLineSegment(sketch, "E43", {"start": v(428.08, 63.7) * mm, "end": v(427.93, 46.8) * mm});
            skSolve(sketch);
        }
        {
            var Q0;
            Q0=makeQuery(id+"F37.imprint","IMPRINT",FACE,{"disambiguationData":[TD([[makeQuery(id+"F37.imprint","IMPRINT",EDGE,{"derivedFrom":sQuery(id+"F37.wireOp",EDGE,"E39")}),1.0]])]});
            extrude(context, id + "F38", {"entities" : qUnion([Q0]), "operationType" : NewBodyOperationType.REMOVE, "oppositeDirection" : true, "depth" : 3.32 * mm});
        }
        {
            var Q0;
            Q0=makeQuery(id+"F1.opExtrude","SWEPT_FACE",FACE,{"disambiguationData":[OSD([sQuery(id+"F0.wireOp",EDGE,"E0.left")])]});
            var sketch = newSketch(context, id + "F39", { "sketchPlane" : qUnion([Q0])});
            skLineSegment(sketch, "E44", {"start": v(-515.01, -16.28) * mm, "end": v(-416.27, -16.28) * mm});
            skLineSegment(sketch, "E45", {"start": v(-416.27, -16.28) * mm, "end": v(-416.27, 61.01) * mm});
            skLineSegment(sketch, "E46", {"start": v(-416.27, 61.01) * mm, "end": v(-434.3, 61.01) * mm});
            skLineSegment(sketch, "E47", {"start": v(-434.3, 61.01) * mm, "end": v(-515.01, -16.28) * mm});
            skSolve(sketch);
        }
        {
            var Q0;
            Q0=makeQuery(id+"F39.imprint","IMPRINT",FACE,{"disambiguationData":[TD([[makeQuery(id+"F39.imprint","IMPRINT",EDGE,{"derivedFrom":sQuery(id+"F39.wireOp",EDGE,"E44")}),1.0]])]});
            extrude(context, id + "F40", {"entities" : qUnion([Q0]), "operationType" : NewBodyOperationType.REMOVE, "oppositeDirection" : true, "depth" : 1.54 * mm});
        }
        {
            var Q0;
            Q0=makeQuery(id+"F15.opExtrude","CAP_FACE",FACE,{"disambiguationData":[OSD([sQuery(id+"F0.wireOp",EDGE,"E0.right")])],"isStart":false});
            var sketch = newSketch(context, id + "F41", { "sketchPlane" : qUnion([Q0])});
            skLineSegment(sketch, "E48.bottom", {"start": v(35.76, 51.75) * mm, "end": v(100.69, 51.75) * mm});
            skLineSegment(sketch, "E48.top", {"start": v(35.76, -7.5) * mm, "end": v(100.69, -7.5) * mm});
            skLineSegment(sketch, "E48.left", {"start": v(35.76, 51.75) * mm, "end": v(35.76, -7.5) * mm});
            skLineSegment(sketch, "E48.right", {"start": v(100.69, 51.75) * mm, "end": v(100.69, -7.5) * mm});
            skLineSegment(sketch, "E49.bottom", {"start": v(234.68, 50.15) * mm, "end": v(293.54, 50.15) * mm});
            skLineSegment(sketch, "E49.top", {"start": v(234.68, -7.79) * mm, "end": v(293.54, -7.79) * mm});
            skLineSegment(sketch, "E49.left", {"start": v(234.68, 50.15) * mm, "end": v(234.68, -7.79) * mm});
            skLineSegment(sketch, "E49.right", {"start": v(293.54, 50.15) * mm, "end": v(293.54, -7.79) * mm});
            skSolve(sketch);
        }
        {
            var Q0;
            Q0=makeQuery(id+"F41.imprint","IMPRINT",FACE,{"disambiguationData":[TD([[makeQuery(id+"F41.imprint","IMPRINT",EDGE,{"derivedFrom":sQuery(id+"F41.wireOp",EDGE,"E48.bottom")}),-1.0]])]});
            var Q1;
            Q1=makeQuery(id+"F41.imprint","IMPRINT",FACE,{"disambiguationData":[TD([[makeQuery(id+"F41.imprint","IMPRINT",EDGE,{"derivedFrom":sQuery(id+"F41.wireOp",EDGE,"E49.bottom")}),-1.0]])]});
            extrude(context, id + "F42", {"entities" : qUnion([Q0, Q1]), "operationType" : NewBodyOperationType.REMOVE, "oppositeDirection" : true, "depth" : 2.18 * mm});
        }
        {
            var Q0;
            Q0=makeQuery(id+"F1.opExtrude","SWEPT_FACE",FACE,{"disambiguationData":[OSD([sQuery(id+"F0.wireOp",EDGE,"E0.left")])]});
            var sketch = newSketch(context, id + "F43", { "sketchPlane" : qUnion([Q0])});
            skLineSegment(sketch, "E50.bottom", {"start": v(-261.24, 48.54) * mm, "end": v(-192.63, 48.54) * mm});
            skLineSegment(sketch, "E50.top", {"start": v(-261.24, -11.72) * mm, "end": v(-192.63, -11.72) * mm});
            skLineSegment(sketch, "E50.left", {"start": v(-261.24, 48.54) * mm, "end": v(-261.24, -11.72) * mm});
            skLineSegment(sketch, "E50.right", {"start": v(-192.63, 48.54) * mm, "end": v(-192.63, -11.72) * mm});
            skLineSegment(sketch, "E51.bottom", {"start": v(-92.24, 48.74) * mm, "end": v(-17.18, 48.74) * mm});
            skLineSegment(sketch, "E51.top", {"start": v(-92.24, -17.67) * mm, "end": v(-17.18, -17.67) * mm});
            skLineSegment(sketch, "E51.left", {"start": v(-92.24, 48.74) * mm, "end": v(-92.24, -17.67) * mm});
            skLineSegment(sketch, "E51.right", {"start": v(-17.18, 48.74) * mm, "end": v(-17.18, -17.67) * mm});
            skSolve(sketch);
        }
        {
            var Q0;
            Q0=makeQuery(id+"F43.imprint","IMPRINT",FACE,{"disambiguationData":[TD([[makeQuery(id+"F43.imprint","IMPRINT",EDGE,{"derivedFrom":sQuery(id+"F43.wireOp",EDGE,"E51.bottom")}),-1.0]])]});
            var Q1;
            Q1=makeQuery(id+"F43.imprint","IMPRINT",FACE,{"disambiguationData":[TD([[makeQuery(id+"F43.imprint","IMPRINT",EDGE,{"derivedFrom":sQuery(id+"F43.wireOp",EDGE,"E50.bottom")}),-1.0]])]});
            extrude(context, id + "F44", {"entities" : qUnion([Q0, Q1]), "operationType" : NewBodyOperationType.REMOVE, "oppositeDirection" : true, "depth" : 7.16 * mm});
        }
        {
            var Q0;
            Q0=makeQuery(id+"F9.opExtrude","CAP_FACE",FACE,{"disambiguationData":[OSD([sQuery(id+"F8.wireOp",EDGE,"E7")])],"isStart":false});
            var sketch = newSketch(context, id + "F45", { "sketchPlane" : qUnion([Q0])});
            skCircle(sketch, "E52", {"center": v(-452.92, -37.34) * mm, "radius": 9.09 * mm});
            skCircle(sketch, "E53", {"center": v(-427.2, -51.3) * mm, "radius": 9.6 * mm});
            skCircle(sketch, "E54", {"center": v(-414.73, -77.27) * mm, "radius": 9.4 * mm});
            skCircle(sketch, "E55", {"center": v(-430.92, -105.46) * mm, "radius": 9.14 * mm});
            skCircle(sketch, "E56", {"center": v(-460.32, -108.4) * mm, "radius": 9.87 * mm});
            skCircle(sketch, "E57", {"center": v(-484.7, -87.85) * mm, "radius": 9.16 * mm});
            skCircle(sketch, "E58", {"center": v(-483.13, -59.03) * mm, "radius": 8.65 * mm});
            skCircle(sketch, "E59", {"center": v(-451.8, -74.82) * mm, "radius": 19.37 * mm});
            skSolve(sketch);
        }
        {
            var Q0;
            Q0=makeQuery(id+"F45.imprint","IMPRINT",FACE,{"disambiguationData":[TD([[makeQuery(id+"F45.imprint","IMPRINT",EDGE,{"derivedFrom":sQuery(id+"F45.wireOp",EDGE,"E54")}),1.0]])]});
            var Q1;
            Q1=makeQuery(id+"F45.imprint","IMPRINT",FACE,{"disambiguationData":[TD([[makeQuery(id+"F45.imprint","IMPRINT",EDGE,{"derivedFrom":sQuery(id+"F45.wireOp",EDGE,"E55")}),1.0]])]});
            var Q2;
            Q2=makeQuery(id+"F45.imprint","IMPRINT",FACE,{"disambiguationData":[TD([[makeQuery(id+"F45.imprint","IMPRINT",EDGE,{"derivedFrom":sQuery(id+"F45.wireOp",EDGE,"E56")}),1.0]])]});
            var Q3;
            Q3=makeQuery(id+"F45.imprint","IMPRINT",FACE,{"disambiguationData":[TD([[makeQuery(id+"F45.imprint","IMPRINT",EDGE,{"derivedFrom":sQuery(id+"F45.wireOp",EDGE,"E57")}),1.0]])]});
            var Q4;
            Q4=makeQuery(id+"F45.imprint","IMPRINT",FACE,{"disambiguationData":[TD([[makeQuery(id+"F45.imprint","IMPRINT",EDGE,{"derivedFrom":sQuery(id+"F45.wireOp",EDGE,"E58")}),1.0]])]});
            var Q5;
            Q5=makeQuery(id+"F45.imprint","IMPRINT",FACE,{"disambiguationData":[TD([[makeQuery(id+"F45.imprint","IMPRINT",EDGE,{"derivedFrom":sQuery(id+"F45.wireOp",EDGE,"E52")}),1.0]])]});
            var Q6;
            Q6=makeQuery(id+"F45.imprint","IMPRINT",FACE,{"disambiguationData":[TD([[makeQuery(id+"F45.imprint","IMPRINT",EDGE,{"derivedFrom":sQuery(id+"F45.wireOp",EDGE,"E53")}),1.0]])]});
            extrude(context, id + "F46", {"entities" : qUnion([Q0, Q1, Q2, Q3, Q4, Q5, Q6]), "operationType" : NewBodyOperationType.REMOVE, "oppositeDirection" : true, "depth" : 28.97 * mm});
        }
        {
            var Q0;
            Q0=makeQuery(id+"F9.opExtrude","CAP_FACE",FACE,{"disambiguationData":[OSD([sQuery(id+"F8.wireOp",EDGE,"E7")])],"isStart":false});
            var sketch = newSketch(context, id + "F47", { "sketchPlane" : qUnion([Q0])});
            skCircle(sketch, "E60", {"center": v(-451.8, -74.82) * mm, "radius": 20.14 * mm});
            skSolve(sketch);
        }
        {
            var Q0;
            Q0=makeQuery(id+"F47.imprint","IMPRINT",FACE,{"disambiguationData":[TD([[makeQuery(id+"F47.imprint","IMPRINT",EDGE,{"derivedFrom":sQuery(id+"F47.wireOp",EDGE,"E60")}),1.0]])]});
            extrude(context, id + "F48", {"entities" : qUnion([Q0]), "operationType" : NewBodyOperationType.REMOVE, "oppositeDirection" : true, "depth" : 35.28 * mm});
        }
        {
            var Q0;
            Q0=makeQuery(id+"F9.opExtrude","CAP_FACE",FACE,{"disambiguationData":[OSD([sQuery(id+"F8.wireOp",EDGE,"E8")])],"isStart":false});
            var sketch = newSketch(context, id + "F49", { "sketchPlane" : qUnion([Q0])});
            skCircle(sketch, "E61", {"center": v(-79.46, -46.73) * mm, "radius": 11.05 * mm});
            skCircle(sketch, "E62", {"center": v(-53.93, -59.72) * mm, "radius": 9.6 * mm});
            skCircle(sketch, "E63", {"center": v(-50.5, -89.2) * mm, "radius": 9.16 * mm});
            skCircle(sketch, "E64", {"center": v(-73.16, -110.45) * mm, "radius": 9.55 * mm});
            skCircle(sketch, "E65", {"center": v(-100.81, -102.7) * mm, "radius": 9.21 * mm});
            skCircle(sketch, "E66", {"center": v(-113.05, -78.8) * mm, "radius": 9.21 * mm});
            skCircle(sketch, "E67", {"center": v(-103.61, -53.83) * mm, "radius": 9.47 * mm});
            skSolve(sketch);
        }
        {
            var Q0;
            Q0=makeQuery(id+"F49.imprint","IMPRINT",FACE,{"disambiguationData":[TD([[makeQuery(id+"F49.imprint","IMPRINT",EDGE,{"derivedFrom":sQuery(id+"F49.wireOp",EDGE,"E61")}),1.0]])]});
            var Q1;
            Q1=makeQuery(id+"F49.imprint","IMPRINT",FACE,{"disambiguationData":[TD([[makeQuery(id+"F49.imprint","IMPRINT",EDGE,{"derivedFrom":sQuery(id+"F49.wireOp",EDGE,"E67")}),1.0]])]});
            var Q2;
            Q2=makeQuery(id+"F49.imprint","IMPRINT",FACE,{"disambiguationData":[TD([[makeQuery(id+"F49.imprint","IMPRINT",EDGE,{"derivedFrom":sQuery(id+"F49.wireOp",EDGE,"E66")}),1.0]])]});
            var Q3;
            Q3=makeQuery(id+"F49.imprint","IMPRINT",FACE,{"disambiguationData":[TD([[makeQuery(id+"F49.imprint","IMPRINT",EDGE,{"derivedFrom":sQuery(id+"F49.wireOp",EDGE,"E65")}),1.0]])]});
            var Q4;
            Q4=makeQuery(id+"F49.imprint","IMPRINT",FACE,{"disambiguationData":[TD([[makeQuery(id+"F49.imprint","IMPRINT",EDGE,{"derivedFrom":sQuery(id+"F49.wireOp",EDGE,"E64")}),1.0]])]});
            var Q5;
            Q5=makeQuery(id+"F49.imprint","IMPRINT",FACE,{"disambiguationData":[TD([[makeQuery(id+"F49.imprint","IMPRINT",EDGE,{"derivedFrom":sQuery(id+"F49.wireOp",EDGE,"E63")}),1.0]])]});
            var Q6;
            Q6=makeQuery(id+"F49.imprint","IMPRINT",FACE,{"disambiguationData":[TD([[makeQuery(id+"F49.imprint","IMPRINT",EDGE,{"derivedFrom":sQuery(id+"F49.wireOp",EDGE,"E62")}),1.0]])]});
            extrude(context, id + "F50", {"entities" : qUnion([Q0, Q1, Q2, Q3, Q4, Q5, Q6]), "operationType" : NewBodyOperationType.REMOVE, "oppositeDirection" : true, "depth" : 10.24 * mm});
        }
        {
            var Q0;
            Q0=makeQuery(id+"F9.opExtrude","CAP_FACE",FACE,{"disambiguationData":[OSD([sQuery(id+"F8.wireOp",EDGE,"E8")])],"isStart":false});
            var sketch = newSketch(context, id + "F51", { "sketchPlane" : qUnion([Q0])});
            skCircle(sketch, "E68", {"center": v(-79.9, -81.93) * mm, "radius": 15 * mm});
            skSolve(sketch);
        }
        {
            var Q0;
            Q0=makeQuery(id+"F51.imprint","IMPRINT",FACE,{"disambiguationData":[TD([[makeQuery(id+"F51.imprint","IMPRINT",EDGE,{"derivedFrom":sQuery(id+"F51.wireOp",EDGE,"E68")}),1.0]])]});
            extrude(context, id + "F52", {"entities" : qUnion([Q0]), "operationType" : NewBodyOperationType.REMOVE, "oppositeDirection" : true, "depth" : 25 * mm});
        }
        {
            var Q0;
            Q0=makeQuery(id+"F15.opExtrude","CAP_FACE",FACE,{"disambiguationData":[OSD([sQuery(id+"F0.wireOp",EDGE,"E0.right")])],"isStart":false});
            var sketch = newSketch(context, id + "F53", { "sketchPlane" : qUnion([Q0])});
            skLineSegment(sketch, "E69", {"start": v(0, -59.96) * mm, "end": v(0, -74.82) * mm});
            skLineSegment(sketch, "E70", {"start": v(0, -74.82) * mm, "end": v(28.3, -74.82) * mm});
            skLineSegment(sketch, "E71", {"start": v(28.3, -74.82) * mm, "end": v(0, -59.96) * mm});
            skSolve(sketch);
        }
        {
            var Q0;
            Q0=makeQuery(id+"F53.imprint","IMPRINT",FACE,{"disambiguationData":[TD([[makeQuery(id+"F53.imprint","IMPRINT",EDGE,{"derivedFrom":sQuery(id+"F53.wireOp",EDGE,"E69")}),1.0]])]});
            extrude(context, id + "F54", {"entities" : qUnion([Q0]), "operationType" : NewBodyOperationType.REMOVE, "oppositeDirection" : true, "depth" : 30.98 * mm});
        }
        {
            var Q0;
            Q0=makeQuery(id+"F54.boolean.opBoolean","COPY",FACE,{"derivedFrom":makeQuery(id+"F54.opExtrude","CAP_FACE",FACE,{"disambiguationData":[OSD([sQuery(id+"F53.wireOp",EDGE,"E69"),sQuery(id+"F53.wireOp",EDGE,"E70"),sQuery(id+"F53.wireOp",EDGE,"E71")])],"isStart":false})});
            extrude(context, id + "F55", {"entities" : qUnion([Q0]), "operationType" : NewBodyOperationType.REMOVE, "oppositeDirection" : true, "depth" : 176.6 * mm});
        }
    });
